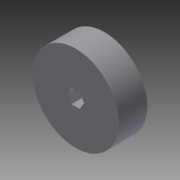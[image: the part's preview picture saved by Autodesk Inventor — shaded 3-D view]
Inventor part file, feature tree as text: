
AUTODESK INVENTOR PART (.ipt)
format: ipt  version: 2014 SP1 (Build 180222100, 222)  size: 80,896 bytes
history: native  units: in
note: dims shown in document units (in); Inventor stores cm internally (conversion verified against a paired STEP export)
features: extrude x1, sketch x1
ambient origin geometry x8: Origin, YZ Plane, XZ Plane, XY Plane, X Axis, Y Axis, Z Axis, Center Point
bodies: Solid1 (feature_tree)
feature tree (2):
  extrude  "Extrusion1"  Depth=0.5in
  sketch  "Sketch1"  dims[d0=3.0in d1=0.5in d2=1.0in d3=0.0in]
